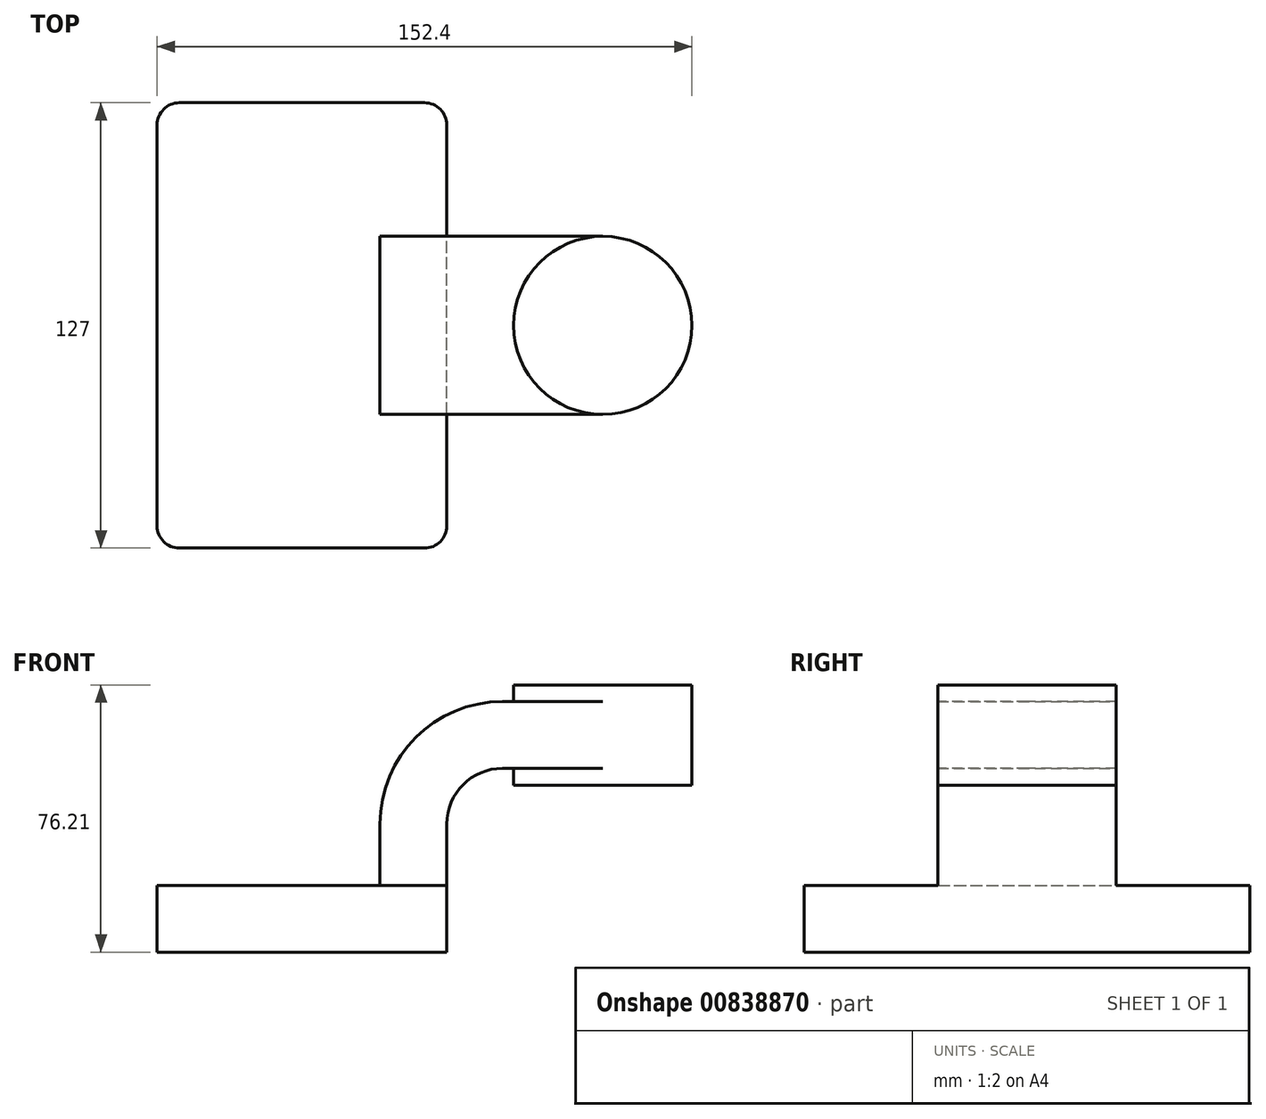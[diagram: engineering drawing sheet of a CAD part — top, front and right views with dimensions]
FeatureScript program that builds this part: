
annotation { "Feature Type Name" : "Feature", "Feature Type Description" : "" }
export const myFeature = defineFeature(function(context is Context, id is Id, definition is map)
    precondition{}
    {
        {
            var Q0;
            Q0=qCreatedBy(makeId("Front.planeOp"),FACE);
            var sketch = newSketch(context, id + "F0", { "sketchPlane" : qUnion([Q0])});
            skLineSegment(sketch, "E0.bottom", {"start": v(-41.27, -9.53) * mm, "end": v(41.28, -9.53) * mm});
            skLineSegment(sketch, "E0.top", {"start": v(-41.28, 9.53) * mm, "end": v(41.28, 9.53) * mm});
            skLineSegment(sketch, "E0.left", {"start": v(-41.27, -9.53) * mm, "end": v(-41.27, 9.53) * mm});
            skLineSegment(sketch, "E0.right", {"start": v(41.28, -9.53) * mm, "end": v(41.28, 9.53) * mm});
            skPoint(sketch, "E0.middle", {"position": v(0, 0) * mm});
            skLineSegment(sketch, "E1.bottom", {"start": v(111.13, 38.1) * mm, "end": v(60.33, 38.1) * mm});
            skLineSegment(sketch, "E1.top", {"start": v(111.13, 66.68) * mm, "end": v(60.33, 66.68) * mm});
            skLineSegment(sketch, "E1.left", {"start": v(111.13, 38.1) * mm, "end": v(111.13, 66.68) * mm});
            skLineSegment(sketch, "E1.right", {"start": v(60.33, 38.1) * mm, "end": v(60.33, 66.68) * mm});
            skPoint(sketch, "E1.middle", {"position": v(85.73, 52.39) * mm});
            skLineSegment(sketch, "E2", {"start": v(41.28, 9.53) * mm, "end": v(41.28, 27) * mm});
            skArc(sketch, "E3", {"start": v(41.28, 27) * mm, "mid": v(45.92, 38.23) * mm, "end": v(57.15, 42.88) * mm});
            skLineSegment(sketch, "E4", {"start": v(57.15, 42.88) * mm, "end": v(85.73, 42.88) * mm});
            skLineSegment(sketch, "E5.0", {"start": v(57.15, 61.93) * mm, "end": v(85.73, 61.93) * mm});
            skArc(sketch, "E5.1", {"start": v(22.23, 27) * mm, "mid": v(32.45, 51.7) * mm, "end": v(57.15, 61.93) * mm});
            skLineSegment(sketch, "E5.2", {"start": v(22.23, 9.53) * mm, "end": v(22.23, 27) * mm});
            skPoint(sketch, "E6", {"position": v(85.73, 38.1) * mm});
            skLineSegment(sketch, "E7", {"start": v(85.73, 38.1) * mm, "end": v(85.73, 66.68) * mm});
            skFitSpline(sketch, "E8", {"points": [v(-41.28, 9.52) * mm, v(57.15, 61.93) * mm], "startDerivative": vector(2.48, 86.17) * mm, "endDerivative": vector(104.57, -7.47) * mm});
            skSolve(sketch);
        }
        {
            var Q0;
            Q0=makeQuery(id+"F0.imprint","IMPRINT",FACE,{"disambiguationData":[TD([[makeQuery(id+"F0.imprint","IMPRINT",EDGE,{"derivedFrom":sQuery(id+"F0.wireOp",EDGE,"E0.bottom")}),1.0]])]});
            extrude(context, id + "F1", {"entities" : qUnion([Q0]), "endBound" : BoundingType.SYMMETRIC, "depth" : 127 * mm, "offsetDistance" : 25.4 * mm});
        }
        {
            var Q0;
            {var subQ1=sQuery(id+"F0.wireOp",EDGE,"E2");Q0=makeQuery(id+"F0.imprint","IMPRINT",FACE,{"disambiguationData":[TD([[makeQuery(id+"F0.imprint","IMPRINT",EDGE,{"derivedFrom":subQ1}),1.0]])]});}
            var Q1;
            {var subQ0=sQuery(id+"F0.wireOp",EDGE,"E4");var subQ1=sQuery(id+"F0.wireOp",EDGE,"E1.right");var subQ2=makeQuery(id+"F0.imprint","INTERSECT",VERTEX,{"derivedFrom":[subQ1,subQ0]});Q1=makeQuery(id+"F0.imprint","IMPRINT",FACE,{"disambiguationData":[TD([[makeQuery(id+"F0.imprint","IMPRINT",EDGE,{"disambiguationData":[TD([[subQ2,-1.0]])],"derivedFrom":subQ1}),-1.0]])]});}
            extrude(context, id + "F2", {"entities" : qUnion([Q0, Q1]), "operationType" : NewBodyOperationType.ADD, "endBound" : BoundingType.SYMMETRIC, "depth" : 50.8 * mm, "offsetDistance" : 25.4 * mm});
        }
        {
            var Q0;
            Q0=makeQuery(id+"F0.imprint","IMPRINT",FACE,{"disambiguationData":[TD([[makeQuery(id+"F0.imprint","IMPRINT",EDGE,{"derivedFrom":sQuery(id+"F0.wireOp",EDGE,"E5.1")}),1.0]])]});
            extrude(context, id + "F3", {"entities" : qUnion([Q0]), "operationType" : NewBodyOperationType.ADD, "endBound" : BoundingType.SYMMETRIC, "depth" : 15.88 * mm, "offsetDistance" : 25.4 * mm});
        }
        {
            var Q0;
            {var subQ4=sQuery(id+"F0.wireOp",EDGE,"E1.left");Q0=makeQuery(id+"F0.imprint","IMPRINT",FACE,{"disambiguationData":[TD([[makeQuery(id+"F0.imprint","IMPRINT",EDGE,{"derivedFrom":subQ4}),1.0]])]});}
            var Q1;
            Q1=sQuery(id+"F0.wireOp",EDGE,"E7");
            revolve(context, id + "F4", {"operationType" : NewBodyOperationType.ADD, "surfaceOperationType" : NewSurfaceOperationType.NEW, "entities" : qUnion([Q0]), "axis" : qUnion([Q1]), "revolveType" : RevolveType.FULL});
        }
        {
            var Q0;
            Q0=makeQuery(id+"F1.opExtrude","CAP_EDGE",EDGE,{"disambiguationData":[OSD([sQuery(id+"F0.wireOp",EDGE,"E0.left")])],"isStart":false});
            var Q1;
            Q1=makeQuery(id+"F1.opExtrude","CAP_EDGE",EDGE,{"disambiguationData":[OSD([sQuery(id+"F0.wireOp",EDGE,"E0.right")])],"isStart":false});
            var Q2;
            Q2=makeQuery(id+"F1.opExtrude","CAP_EDGE",EDGE,{"disambiguationData":[OSD([sQuery(id+"F0.wireOp",EDGE,"E0.left")])],"isStart":true});
            var Q3;
            Q3=makeQuery(id+"F1.opExtrude","CAP_EDGE",EDGE,{"disambiguationData":[OSD([sQuery(id+"F0.wireOp",EDGE,"E0.right")])],"isStart":true});
            fillet(context, id + "F5", {"entities" : qUnion([Q0, Q1, Q2, Q3]), "radius" : 6.35 * mm, "tangentPropagation" : true, "allowEdgeOverflow" : false});
        }
    });
